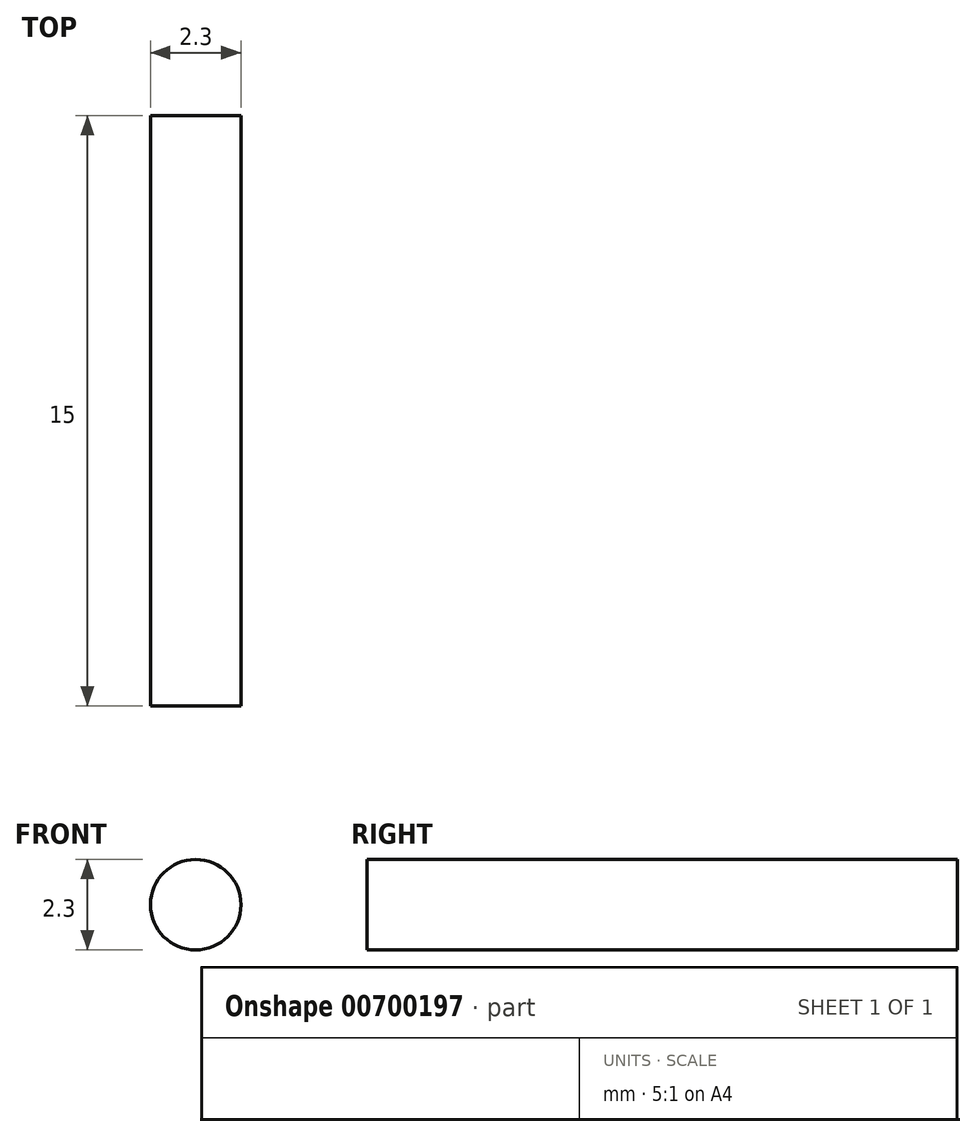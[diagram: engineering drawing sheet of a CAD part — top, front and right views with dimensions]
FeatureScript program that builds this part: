
annotation { "Feature Type Name" : "Feature", "Feature Type Description" : "" }
export const myFeature = defineFeature(function(context is Context, id is Id, definition is map)
    precondition{}
    {
        {
            var Q0;
            Q0=qCreatedBy(makeId("Front.planeOp"),FACE);
            var sketch = newSketch(context, id + "F0", { "sketchPlane" : qUnion([Q0])});
            skCircle(sketch, "E0", {"center": v(0, 0) * mm, "radius": 1.15 * mm});
            skSolve(sketch);
        }
        {
            var Q0;
            Q0=qSketchRegion(id+"F0",true);
            extrude(context, id + "F1", {"entities" : qUnion([Q0]), "depth" : 15 * mm, "offsetDistance" : 25 * mm});
        }
    });
